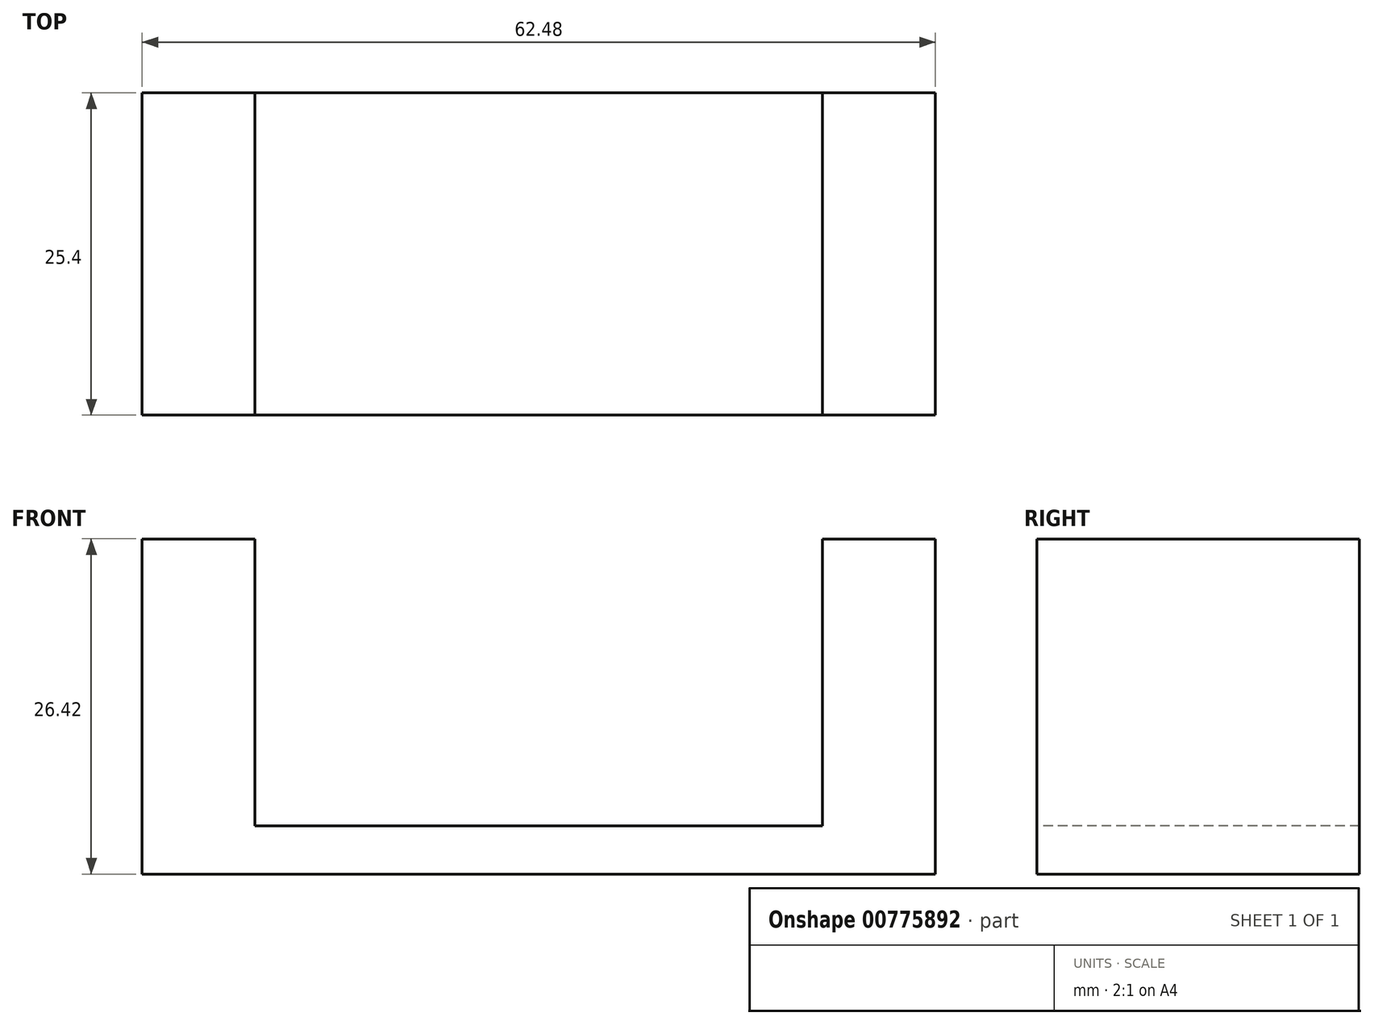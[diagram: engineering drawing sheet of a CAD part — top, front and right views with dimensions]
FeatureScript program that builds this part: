
annotation { "Feature Type Name" : "Feature", "Feature Type Description" : "" }
export const myFeature = defineFeature(function(context is Context, id is Id, definition is map)
    precondition{}
    {
        {
            var Q0;
            Q0=qCreatedBy(makeId("Top.planeOp"),FACE);
            var sketch = newSketch(context, id + "F0", { "sketchPlane" : qUnion([Q0])});
            skLineSegment(sketch, "E0.bottom", {"start": v(27.43, -12.7) * mm, "end": v(-27.43, -12.7) * mm});
            skLineSegment(sketch, "E0.top", {"start": v(27.43, 12.7) * mm, "end": v(-27.43, 12.7) * mm});
            skLineSegment(sketch, "E0.left", {"start": v(27.43, -12.7) * mm, "end": v(27.43, 12.7) * mm});
            skLineSegment(sketch, "E0.right", {"start": v(-27.43, -12.7) * mm, "end": v(-27.43, 12.7) * mm});
            skPoint(sketch, "E0.middle", {"position": v(0, 0) * mm});
            skSolve(sketch);
        }
        {
            var Q0;
            Q0=makeQuery(id+"F0.imprint","IMPRINT",FACE,{"disambiguationData":[TD([[makeQuery(id+"F0.imprint","IMPRINT",EDGE,{"derivedFrom":sQuery(id+"F0.wireOp",EDGE,"E0.bottom")}),-1.0]])]});
            extrude(context, id + "F1", {"entities" : qUnion([Q0]), "depth" : 3.8 * mm});
        }
        {
            var Q0;
            Q0=makeQuery(id+"F1.opExtrude","CAP_FACE",FACE,{"disambiguationData":[OSD([sQuery(id+"F0.wireOp",EDGE,"E0.bottom"),sQuery(id+"F0.wireOp",EDGE,"E0.top"),sQuery(id+"F0.wireOp",EDGE,"E0.left"),sQuery(id+"F0.wireOp",EDGE,"E0.right")])],"isStart":false});
            var sketch = newSketch(context, id + "F2", { "sketchPlane" : qUnion([Q0])});
            skLineSegment(sketch, "E1.bottom", {"start": v(-27.43, 12.7) * mm, "end": v(-22.35, 12.7) * mm});
            skLineSegment(sketch, "E1.top", {"start": v(-27.43, -12.7) * mm, "end": v(-22.35, -12.7) * mm});
            skLineSegment(sketch, "E1.left", {"start": v(-27.43, 12.7) * mm, "end": v(-27.43, -12.7) * mm});
            skLineSegment(sketch, "E1.right", {"start": v(-22.35, 12.7) * mm, "end": v(-22.35, -12.7) * mm});
            skLineSegment(sketch, "E2.bottom", {"start": v(22.35, 12.7) * mm, "end": v(27.43, 12.7) * mm});
            skLineSegment(sketch, "E2.top", {"start": v(22.35, -12.7) * mm, "end": v(27.43, -12.7) * mm});
            skLineSegment(sketch, "E2.left", {"start": v(22.35, 12.7) * mm, "end": v(22.35, -12.7) * mm});
            skLineSegment(sketch, "E2.right", {"start": v(27.43, 12.7) * mm, "end": v(27.43, -12.7) * mm});
            skSolve(sketch);
        }
        {
            var Q0;
            Q0=makeQuery(id+"F2.imprint","IMPRINT",FACE,{"disambiguationData":[TD([[makeQuery(id+"F2.imprint","IMPRINT",EDGE,{"derivedFrom":sQuery(id+"F2.wireOp",EDGE,"E1.bottom")}),1.0]])]});
            var Q1;
            Q1=makeQuery(id+"F2.imprint","IMPRINT",FACE,{"disambiguationData":[TD([[makeQuery(id+"F2.imprint","IMPRINT",EDGE,{"derivedFrom":sQuery(id+"F2.wireOp",EDGE,"E2.bottom")}),1.0]])]});
            extrude(context, id + "F3", {"entities" : qUnion([Q0, Q1]), "operationType" : NewBodyOperationType.ADD, "depth" : 22.6 * mm});
        }
        {
            var Q0;
            Q0=makeQuery(id+"F3.boolean.opBoolean","MERGE",FACE,{"derivedFrom":[makeQuery(id+"F1.opExtrude","SWEPT_FACE",FACE,{"disambiguationData":[OSD([sQuery(id+"F0.wireOp",EDGE,"E0.right")])]}),makeQuery(id+"F3.opExtrude","SWEPT_FACE",FACE,{"disambiguationData":[OSD([sQuery(id+"F2.wireOp",EDGE,"E1.left")])]})]});
            var sketch = newSketch(context, id + "F4", { "sketchPlane" : qUnion([Q0])});
            skLineSegment(sketch, "E3.bottom", {"start": v(-12.7, 26.42) * mm, "end": v(12.7, 26.42) * mm});
            skLineSegment(sketch, "E3.top", {"start": v(-12.7, 22.6) * mm, "end": v(12.7, 22.6) * mm});
            skLineSegment(sketch, "E3.left", {"start": v(-12.7, 26.42) * mm, "end": v(-12.7, 22.6) * mm});
            skLineSegment(sketch, "E3.right", {"start": v(12.7, 26.42) * mm, "end": v(12.7, 22.6) * mm});
            skSolve(sketch);
        }
        {
            var Q0;
            Q0=makeQuery(id+"F3.boolean.opBoolean","MERGE",FACE,{"derivedFrom":[makeQuery(id+"F1.opExtrude","SWEPT_FACE",FACE,{"disambiguationData":[OSD([sQuery(id+"F0.wireOp",EDGE,"E0.left")])]}),makeQuery(id+"F3.opExtrude","SWEPT_FACE",FACE,{"disambiguationData":[OSD([sQuery(id+"F2.wireOp",EDGE,"E2.right")])]})]});
            var sketch = newSketch(context, id + "F5", { "sketchPlane" : qUnion([Q0])});
            skLineSegment(sketch, "E4.bottom", {"start": v(-12.7, 26.42) * mm, "end": v(12.7, 26.42) * mm});
            skLineSegment(sketch, "E4.top", {"start": v(-12.7, 22.6) * mm, "end": v(12.7, 22.6) * mm});
            skLineSegment(sketch, "E4.left", {"start": v(-12.7, 26.42) * mm, "end": v(-12.7, 22.6) * mm});
            skLineSegment(sketch, "E4.right", {"start": v(12.7, 26.42) * mm, "end": v(12.7, 22.6) * mm});
            skSolve(sketch);
        }
        {
            var Q0;
            {var subQ0=sQuery(id+"F5.wireOp",EDGE,"E4.top");Q0=makeQuery(id+"F5.imprint","IMPRINT",FACE,{"disambiguationData":[TD([[makeQuery(id+"F5.imprint","IMPRINT",EDGE,{"derivedFrom":subQ0}),-1.0]])]});}
            var Q1;
            Q1=makeQuery(id+"F5.imprint","IMPRINT",FACE,{"disambiguationData":[TD([[makeQuery(id+"F5.imprint","IMPRINT",EDGE,{"derivedFrom":sQuery(id+"F5.wireOp",EDGE,"E4.bottom")}),-1.0]])]});
            extrude(context, id + "F6", {"entities" : qUnion([Q0, Q1]), "operationType" : NewBodyOperationType.ADD, "depth" : 3.8 * mm});
        }
        {
            var Q0;
            Q0=makeQuery(id+"F4.imprint","IMPRINT",FACE,{"disambiguationData":[TD([[makeQuery(id+"F4.imprint","IMPRINT",EDGE,{"derivedFrom":sQuery(id+"F4.wireOp",EDGE,"E3.bottom")}),1.0]])]});
            var Q1;
            {var subQ0=sQuery(id+"F4.wireOp",EDGE,"E3.top");Q1=makeQuery(id+"F4.imprint","IMPRINT",FACE,{"disambiguationData":[TD([[makeQuery(id+"F4.imprint","IMPRINT",EDGE,{"derivedFrom":subQ0}),-1.0]])]});}
            extrude(context, id + "F7", {"entities" : qUnion([Q0, Q1]), "operationType" : NewBodyOperationType.ADD, "depth" : 3.8 * mm});
        }
    });
